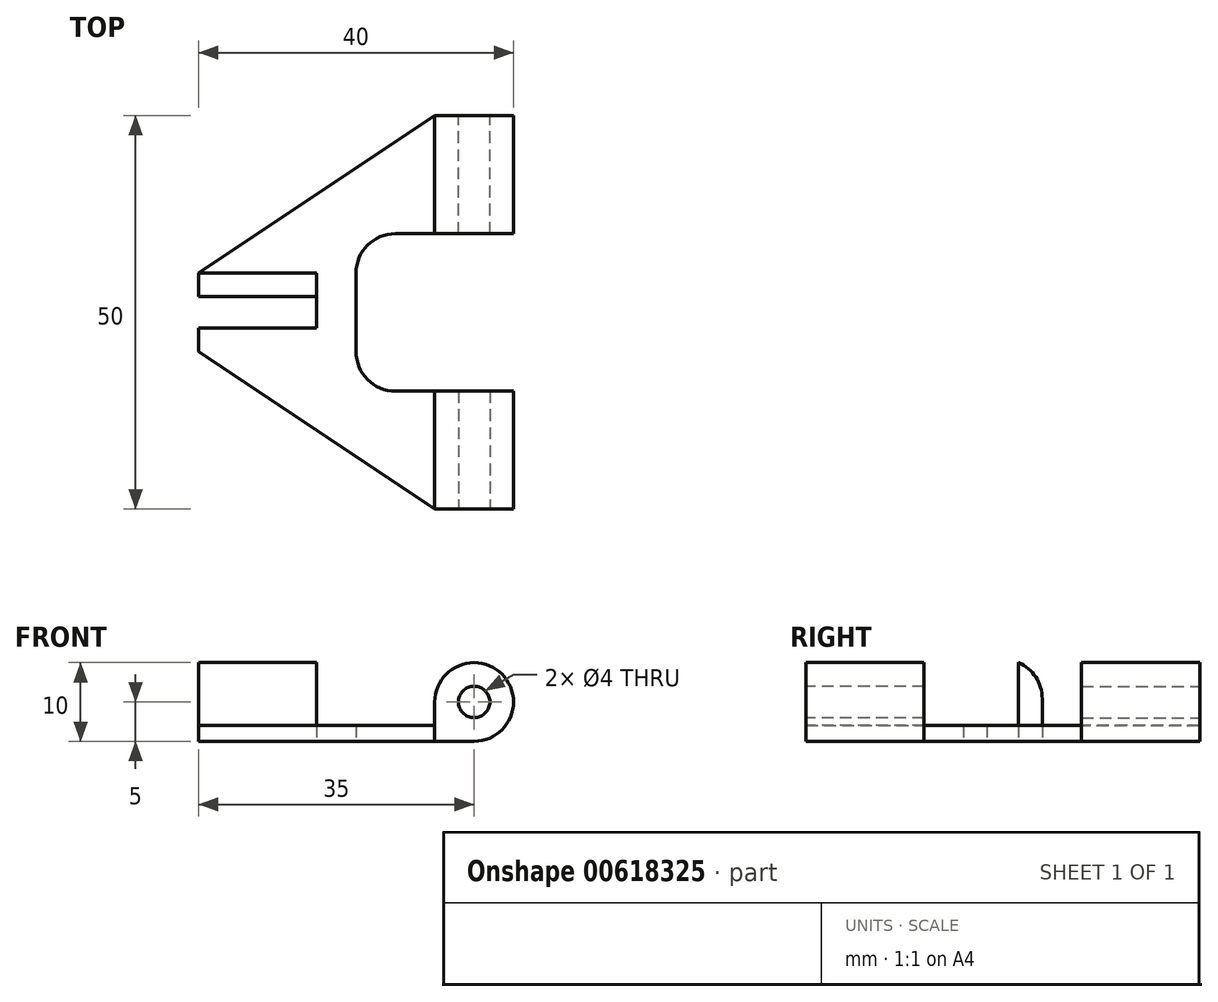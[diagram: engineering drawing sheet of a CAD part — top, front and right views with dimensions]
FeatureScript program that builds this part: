
annotation { "Feature Type Name" : "Feature", "Feature Type Description" : "" }
export const myFeature = defineFeature(function(context is Context, id is Id, definition is map)
    precondition{}
    {
        {
            var Q0;
            Q0=qCreatedBy(makeId("Top.planeOp"),FACE);
            var sketch = newSketch(context, id + "F0", { "sketchPlane" : qUnion([Q0])});
            skLineSegment(sketch, "E0", {"start": v(-30, 0) * mm, "end": v(-30, 5) * mm});
            skLineSegment(sketch, "E1", {"start": v(-30, 5) * mm, "end": v(0, 25) * mm});
            skLineSegment(sketch, "E2", {"start": v(0, 25) * mm, "end": v(0, 0) * mm});
            skLineSegment(sketch, "E3", {"start": v(0, 0) * mm, "end": v(0, -25) * mm});
            skLineSegment(sketch, "E4", {"start": v(0, -25) * mm, "end": v(-30, -5) * mm});
            skLineSegment(sketch, "E5", {"start": v(-30, -5) * mm, "end": v(-30, 0) * mm});
            skLineSegment(sketch, "E6.bottom", {"start": v(-30, -5) * mm, "end": v(-15, -5) * mm});
            skLineSegment(sketch, "E6.top", {"start": v(-30, 5) * mm, "end": v(-15, 5) * mm});
            skLineSegment(sketch, "E6.left", {"start": v(-30, -5) * mm, "end": v(-30, 5) * mm});
            skLineSegment(sketch, "E6.right", {"start": v(-15, -5) * mm, "end": v(-15, 5) * mm});
            skLineSegment(sketch, "E7", {"start": v(-30, 0) * mm, "end": v(-30, 2) * mm});
            skLineSegment(sketch, "E8", {"start": v(-30, 2) * mm, "end": v(-15, 2) * mm});
            skLineSegment(sketch, "E9", {"start": v(-15, 2) * mm, "end": v(-15, -2) * mm});
            skLineSegment(sketch, "E10", {"start": v(-15, -2) * mm, "end": v(-30, -2) * mm});
            skLineSegment(sketch, "E11", {"start": v(-30, -2) * mm, "end": v(-30, 0) * mm});
            skLineSegment(sketch, "E12.bottom", {"start": v(-10, 10) * mm, "end": v(10, 10) * mm});
            skLineSegment(sketch, "E12.top", {"start": v(-10, -10) * mm, "end": v(10, -10) * mm});
            skLineSegment(sketch, "E12.left", {"start": v(-10, 10) * mm, "end": v(-10, -10) * mm});
            skLineSegment(sketch, "E12.right", {"start": v(10, 10) * mm, "end": v(10, -10) * mm});
            skPoint(sketch, "E12.middle", {"position": v(0, 0) * mm});
            skSolve(sketch);
        }
        {
            var Q0;
            {var subQ8=sQuery(id+"F0.wireOp",EDGE,"E1");Q0=makeQuery(id+"F0.imprint","IMPRINT",FACE,{"disambiguationData":[TD([[makeQuery(id+"F0.imprint","IMPRINT",EDGE,{"derivedFrom":subQ8}),-1.0]])]});}
            var Q1;
            {var subQ0=sQuery(id+"F0.wireOp",EDGE,"E6.top");Q1=makeQuery(id+"F0.imprint","IMPRINT",FACE,{"disambiguationData":[TD([[makeQuery(id+"F0.imprint","IMPRINT",EDGE,{"derivedFrom":subQ0}),-1.0]])]});}
            var Q2;
            Q2=makeQuery(id+"F0.imprint","IMPRINT",FACE,{"disambiguationData":[TD([[makeQuery(id+"F0.imprint","IMPRINT",EDGE,{"derivedFrom":sQuery(id+"F0.wireOp",EDGE,"E7")}),-1.0]])]});
            var Q3;
            {var subQ0=sQuery(id+"F0.wireOp",EDGE,"E6.bottom");Q3=makeQuery(id+"F0.imprint","IMPRINT",FACE,{"disambiguationData":[TD([[makeQuery(id+"F0.imprint","IMPRINT",EDGE,{"derivedFrom":subQ0}),1.0]])]});}
            extrude(context, id + "F1", {"entities" : qUnion([Q0, Q1, Q2, Q3]), "depth" : 2 * mm, "offsetDistance" : 25 * mm});
        }
        {
            var Q0;
            Q0=makeQuery(id+"F1.opExtrude","CAP_FACE",FACE,{"disambiguationData":[OSD([sQuery(id+"F0.wireOp",EDGE,"E1"),sQuery(id+"F0.wireOp",EDGE,"E2"),sQuery(id+"F0.wireOp",EDGE,"E3"),sQuery(id+"F0.wireOp",EDGE,"E4"),sQuery(id+"F0.wireOp",EDGE,"E6.left"),sQuery(id+"F0.wireOp",EDGE,"E7"),sQuery(id+"F0.wireOp",EDGE,"E11"),sQuery(id+"F0.wireOp",EDGE,"E12.bottom"),sQuery(id+"F0.wireOp",EDGE,"E12.top"),sQuery(id+"F0.wireOp",EDGE,"E12.left")])],"isStart":false});
            var sketch = newSketch(context, id + "F2", { "sketchPlane" : qUnion([Q0])});
            skLineSegment(sketch, "E13.bottom", {"start": v(-30, 5) * mm, "end": v(-15, 5) * mm});
            skLineSegment(sketch, "E13.top", {"start": v(-30, -5) * mm, "end": v(-15, -5) * mm});
            skLineSegment(sketch, "E13.left", {"start": v(-30, 5) * mm, "end": v(-30, -5) * mm});
            skLineSegment(sketch, "E13.right", {"start": v(-15, 5) * mm, "end": v(-15, -5) * mm});
            skSolve(sketch);
        }
        {
            var Q0;
            Q0=makeQuery(id+"F2.imprint","IMPRINT",FACE,{"disambiguationData":[TD([[makeQuery(id+"F2.imprint","IMPRINT",EDGE,{"derivedFrom":sQuery(id+"F2.wireOp",EDGE,"E13.bottom")}),-1.0]])]});
            extrude(context, id + "F3", {"entities" : qUnion([Q0]), "operationType" : NewBodyOperationType.ADD, "depth" : 8 * mm, "offsetDistance" : 25 * mm});
        }
        {
            var Q0;
            Q0=makeQuery(id+"F3.boolean.opBoolean","MERGE",FACE,{"derivedFrom":[makeQuery(id+"F1.opExtrude","SWEPT_FACE",FACE,{"disambiguationData":[OSD([sQuery(id+"F0.wireOp",EDGE,"E6.left"),sQuery(id+"F0.wireOp",EDGE,"E7"),sQuery(id+"F0.wireOp",EDGE,"E11")])]}),makeQuery(id+"F3.opExtrude","SWEPT_FACE",FACE,{"disambiguationData":[OSD([sQuery(id+"F2.wireOp",EDGE,"E13.left")])]})]});
            var sketch = newSketch(context, id + "F4", { "sketchPlane" : qUnion([Q0])});
            skCircle(sketch, "E14", {"center": v(0, 5) * mm, "radius": 2 * mm});
            skSolve(sketch);
        }
        {
            var Q0;
            Q0=makeQuery(id+"F4.imprint","IMPRINT",FACE,{"disambiguationData":[TD([[makeQuery(id+"F4.imprint","IMPRINT",EDGE,{"derivedFrom":sQuery(id+"F4.wireOp",EDGE,"E14")}),1.0]])]});
            extrude(context, id + "F5", {"entities" : qUnion([Q0]), "operationType" : NewBodyOperationType.REMOVE, "oppositeDirection" : true, "depth" : 25 * mm, "offsetDistance" : 25 * mm});
        }
        {
            var Q0;
            Q0=makeQuery(id+"F3.opExtrude","CAP_EDGE",EDGE,{"disambiguationData":[OSD([sQuery(id+"F2.wireOp",EDGE,"E13.top")])],"isStart":false});
            var Q1;
            Q1=makeQuery(id+"F3.opExtrude","CAP_EDGE",EDGE,{"disambiguationData":[OSD([sQuery(id+"F2.wireOp",EDGE,"E13.bottom")])],"isStart":false});
            fillet(context, id + "F6", {"entities" : qUnion([Q0, Q1]), "radius" : 5 * mm, "tangentPropagation" : true, "allowEdgeOverflow" : false});
        }
        {
            var Q0;
            Q0=makeQuery(id+"F1.opExtrude","SWEPT_FACE",FACE,{"disambiguationData":[OSD([sQuery(id+"F0.wireOp",EDGE,"E3")])]});
            var sketch = newSketch(context, id + "F7", { "sketchPlane" : qUnion([Q0])});
            skLineSegment(sketch, "E15.bottom", {"start": v(-10, 0) * mm, "end": v(-25, 0) * mm});
            skLineSegment(sketch, "E15.top", {"start": v(-10, 10) * mm, "end": v(-25, 10) * mm});
            skLineSegment(sketch, "E15.left", {"start": v(-10, 0) * mm, "end": v(-10, 10) * mm});
            skLineSegment(sketch, "E15.right", {"start": v(-25, 0) * mm, "end": v(-25, 10) * mm});
            skSolve(sketch);
        }
        {
            var Q0;
            {var subQ0=sQuery(id+"F7.wireOp",EDGE,"E15.top");Q0=makeQuery(id+"F7.imprint","IMPRINT",FACE,{"disambiguationData":[TD([[makeQuery(id+"F7.imprint","IMPRINT",EDGE,{"derivedFrom":subQ0}),1.0]])]});}
            var Q1;
            {var subQ0=sQuery(id+"F7.wireOp",EDGE,"E15.bottom");Q1=makeQuery(id+"F7.imprint","IMPRINT",FACE,{"disambiguationData":[TD([[makeQuery(id+"F7.imprint","IMPRINT",EDGE,{"derivedFrom":subQ0}),-1.0]])]});}
            extrude(context, id + "F8", {"entities" : qUnion([Q0, Q1]), "operationType" : NewBodyOperationType.ADD, "depth" : 10 * mm, "offsetDistance" : 25 * mm});
        }
        {
            var Q0;
            Q0=makeQuery(id+"F8.opExtrude","CAP_EDGE",EDGE,{"disambiguationData":[OSD([sQuery(id+"F7.wireOp",EDGE,"E15.top")])],"isStart":true});
            var Q1;
            Q1=makeQuery(id+"F8.opExtrude","CAP_EDGE",EDGE,{"disambiguationData":[OSD([sQuery(id+"F7.wireOp",EDGE,"E15.top")])],"isStart":false});
            var Q2;
            Q2=makeQuery(id+"F8.opExtrude","CAP_EDGE",EDGE,{"disambiguationData":[OSD([sQuery(id+"F7.wireOp",EDGE,"E15.bottom")])],"isStart":false});
            fillet(context, id + "F9", {"entities" : qUnion([Q0, Q1, Q2]), "radius" : 5 * mm, "tangentPropagation" : true, "allowEdgeOverflow" : false});
        }
        {
            var Q0;
            Q0=makeQuery(id+"F8.opExtrude","SWEPT_FACE",FACE,{"disambiguationData":[OSD([sQuery(id+"F7.wireOp",EDGE,"E15.right")])]});
            var sketch = newSketch(context, id + "F10", { "sketchPlane" : qUnion([Q0])});
            skCircle(sketch, "E16", {"center": v(5, 5) * mm, "radius": 2 * mm});
            skSolve(sketch);
        }
        {
            var Q0;
            Q0=makeQuery(id+"F10.imprint","IMPRINT",FACE,{"disambiguationData":[TD([[makeQuery(id+"F10.imprint","IMPRINT",EDGE,{"derivedFrom":sQuery(id+"F10.wireOp",EDGE,"E16")}),1.0]])]});
            extrude(context, id + "F11", {"entities" : qUnion([Q0]), "operationType" : NewBodyOperationType.REMOVE, "oppositeDirection" : true, "depth" : 25 * mm, "offsetDistance" : 25 * mm});
        }
        {
            var Q0;
            Q0=makeQuery(id+"F1.opExtrude","SWEPT_FACE",FACE,{"disambiguationData":[OSD([sQuery(id+"F0.wireOp",EDGE,"E2")])]});
            var sketch = newSketch(context, id + "F12", { "sketchPlane" : qUnion([Q0])});
            skLineSegment(sketch, "E17.bottom", {"start": v(25, 0) * mm, "end": v(10, 0) * mm});
            skLineSegment(sketch, "E17.top", {"start": v(25, 10) * mm, "end": v(10, 10) * mm});
            skLineSegment(sketch, "E17.left", {"start": v(25, 0) * mm, "end": v(25, 10) * mm});
            skLineSegment(sketch, "E17.right", {"start": v(10, 0) * mm, "end": v(10, 10) * mm});
            skSolve(sketch);
        }
        {
            var Q0;
            {var subQ0=sQuery(id+"F12.wireOp",EDGE,"E17.bottom");Q0=makeQuery(id+"F12.imprint","IMPRINT",FACE,{"disambiguationData":[TD([[makeQuery(id+"F12.imprint","IMPRINT",EDGE,{"derivedFrom":subQ0}),-1.0]])]});}
            var Q1;
            {var subQ0=sQuery(id+"F12.wireOp",EDGE,"E17.top");Q1=makeQuery(id+"F12.imprint","IMPRINT",FACE,{"disambiguationData":[TD([[makeQuery(id+"F12.imprint","IMPRINT",EDGE,{"derivedFrom":subQ0}),1.0]])]});}
            extrude(context, id + "F13", {"entities" : qUnion([Q0, Q1]), "operationType" : NewBodyOperationType.ADD, "depth" : 10 * mm, "offsetDistance" : 25 * mm});
        }
        {
            var Q0;
            Q0=makeQuery(id+"F13.opExtrude","CAP_EDGE",EDGE,{"disambiguationData":[OSD([sQuery(id+"F12.wireOp",EDGE,"E17.top")])],"isStart":true});
            var Q1;
            Q1=makeQuery(id+"F13.opExtrude","CAP_EDGE",EDGE,{"disambiguationData":[OSD([sQuery(id+"F12.wireOp",EDGE,"E17.top")])],"isStart":false});
            var Q2;
            Q2=makeQuery(id+"F13.opExtrude","CAP_EDGE",EDGE,{"disambiguationData":[OSD([sQuery(id+"F12.wireOp",EDGE,"E17.bottom")])],"isStart":false});
            fillet(context, id + "F14", {"entities" : qUnion([Q0, Q1, Q2]), "radius" : 5 * mm, "tangentPropagation" : true, "allowEdgeOverflow" : false});
        }
        {
            var Q0;
            Q0=makeQuery(id+"F13.opExtrude","SWEPT_FACE",FACE,{"disambiguationData":[OSD([sQuery(id+"F12.wireOp",EDGE,"E17.left")])]});
            var sketch = newSketch(context, id + "F15", { "sketchPlane" : qUnion([Q0])});
            skCircle(sketch, "E18", {"center": v(-5, 5) * mm, "radius": 2 * mm});
            skSolve(sketch);
        }
        {
            var Q0;
            Q0=makeQuery(id+"F15.imprint","IMPRINT",FACE,{"disambiguationData":[TD([[makeQuery(id+"F15.imprint","IMPRINT",EDGE,{"derivedFrom":sQuery(id+"F15.wireOp",EDGE,"E18")}),1.0]])]});
            extrude(context, id + "F16", {"entities" : qUnion([Q0]), "operationType" : NewBodyOperationType.REMOVE, "oppositeDirection" : true, "depth" : 25 * mm, "offsetDistance" : 25 * mm});
        }
        {
            var Q0;
            Q0=makeQuery(id+"F1.opExtrude","SWEPT_EDGE",EDGE,{"disambiguationData":[OSD([sQuery(id+"F0.wireOp",EDGE,"E12.bottom"),sQuery(id+"F0.wireOp",EDGE,"E12.left")])]});
            var Q1;
            Q1=makeQuery(id+"F1.opExtrude","SWEPT_EDGE",EDGE,{"disambiguationData":[OSD([sQuery(id+"F0.wireOp",EDGE,"E12.top"),sQuery(id+"F0.wireOp",EDGE,"E12.left")])]});
            fillet(context, id + "F17", {"entities" : qUnion([Q0, Q1]), "radius" : 5 * mm, "tangentPropagation" : true, "allowEdgeOverflow" : false});
        }
    });
